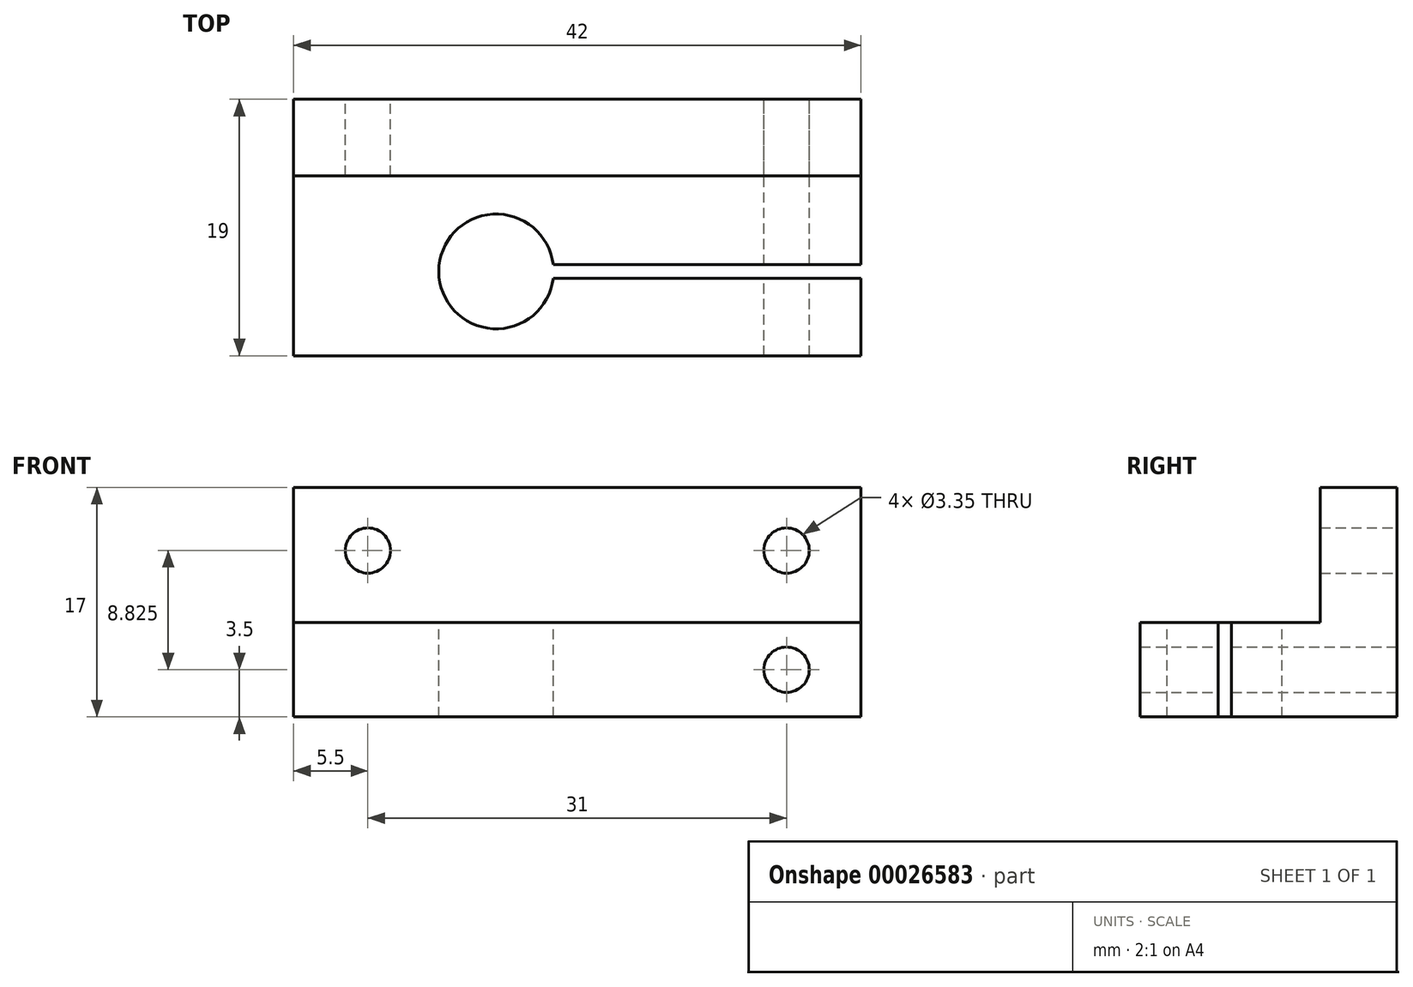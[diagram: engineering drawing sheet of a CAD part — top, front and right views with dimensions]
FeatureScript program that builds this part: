
annotation { "Feature Type Name" : "Feature", "Feature Type Description" : "" }
export const myFeature = defineFeature(function(context is Context, id is Id, definition is map)
    precondition{}
    {
        {
            var Q0;
            Q0=qCreatedBy(makeId("Top.planeOp"),FACE);
            var sketch = newSketch(context, id + "F0", { "sketchPlane" : qUnion([Q0])});
            skLineSegment(sketch, "E0.bottom", {"start": v(0, 0) * mm, "end": v(42, 0) * mm});
            skLineSegment(sketch, "E0.top", {"start": v(0, 19) * mm, "end": v(42, 19) * mm});
            skLineSegment(sketch, "E0.left", {"start": v(0, 0) * mm, "end": v(0, 19) * mm});
            skLineSegment(sketch, "E0.right", {"start": v(42, 0) * mm, "end": v(42, 19) * mm});
            skSolve(sketch);
        }
        {
            var Q0;
            Q0=qSketchRegion(id+"F0",true);
            extrude(context, id + "F1", {"entities" : qUnion([Q0]), "depth" : 7 * mm});
        }
        {
            var Q0;
            Q0=makeQuery(id+"F1.opExtrude","CAP_FACE",FACE,{"disambiguationData":[OSD([sQuery(id+"F0.wireOp",EDGE,"E0.bottom"),sQuery(id+"F0.wireOp",EDGE,"E0.top"),sQuery(id+"F0.wireOp",EDGE,"E0.left"),sQuery(id+"F0.wireOp",EDGE,"E0.right")])],"isStart":false});
            var sketch = newSketch(context, id + "F2", { "sketchPlane" : qUnion([Q0])});
            skCircle(sketch, "E1", {"center": v(15, 6.25) * mm, "radius": 4.25 * mm});
            skLineSegment(sketch, "E2", {"start": v(15, 6.25) * mm, "end": v(42, 6.25) * mm});
            skLineSegment(sketch, "E3", {"start": v(42, 6.25) * mm, "end": v(42, 5.75) * mm});
            skLineSegment(sketch, "E4", {"start": v(42, 5.75) * mm, "end": v(19.22, 5.75) * mm});
            skLineSegment(sketch, "E5", {"start": v(42, 6.25) * mm, "end": v(42, 6.75) * mm});
            skLineSegment(sketch, "E6", {"start": v(42, 6.75) * mm, "end": v(19.22, 6.75) * mm});
            skSolve(sketch);
        }
        {
            var Q0;
            Q0=makeQuery(id+"F1.opExtrude","SWEPT_FACE",FACE,{"disambiguationData":[OSD([sQuery(id+"F0.wireOp",EDGE,"E0.top")])]});
            var sketch = newSketch(context, id + "F3", { "sketchPlane" : qUnion([Q0])});
            skCircle(sketch, "E7", {"center": v(-36.5, 3.5) * mm, "radius": 1.68 * mm});
            skLineSegment(sketch, "E8", {"start": v(-36.5, 3.5) * mm, "end": v(-42, 3.5) * mm});
            skSolve(sketch);
        }
        {
            var Q0;
            Q0=qSketchRegion(id+"F3",true);
            extrude(context, id + "F4", {"entities" : qUnion([Q0]), "operationType" : NewBodyOperationType.REMOVE, "oppositeDirection" : true, "depth" : 25 * mm});
        }
        {
            var Q0;
            Q0=makeQuery(id+"F1.opExtrude","CAP_FACE",FACE,{"disambiguationData":[OSD([sQuery(id+"F0.wireOp",EDGE,"E0.bottom"),sQuery(id+"F0.wireOp",EDGE,"E0.top"),sQuery(id+"F0.wireOp",EDGE,"E0.left"),sQuery(id+"F0.wireOp",EDGE,"E0.right")])],"isStart":false});
            var sketch = newSketch(context, id + "F5", { "sketchPlane" : qUnion([Q0])});
            skLineSegment(sketch, "E9.bottom", {"start": v(0, 19) * mm, "end": v(42, 19) * mm});
            skLineSegment(sketch, "E9.top", {"start": v(0, 13.33) * mm, "end": v(42, 13.33) * mm});
            skLineSegment(sketch, "E9.left", {"start": v(0, 19) * mm, "end": v(0, 13.33) * mm});
            skLineSegment(sketch, "E9.right", {"start": v(42, 19) * mm, "end": v(42, 13.33) * mm});
            skSolve(sketch);
        }
        {
            var Q0;
            Q0=makeQuery(id+"F5.imprint","IMPRINT",FACE,{"disambiguationData":[TD([[makeQuery(id+"F5.imprint","IMPRINT",EDGE,{"derivedFrom":sQuery(id+"F5.wireOp",EDGE,"E9.bottom")}),-1.0]])]});
            extrude(context, id + "F6", {"entities" : qUnion([Q0]), "operationType" : NewBodyOperationType.ADD, "depth" : 10 * mm});
        }
        {
            var Q0;
            Q0=makeQuery(id+"F6.boolean.opBoolean","MERGE",FACE,{"derivedFrom":[makeQuery(id+"F1.opExtrude","SWEPT_FACE",FACE,{"disambiguationData":[OSD([sQuery(id+"F0.wireOp",EDGE,"E0.top")])]}),makeQuery(id+"F6.opExtrude","SWEPT_FACE",FACE,{"disambiguationData":[OSD([sQuery(id+"FFFDCbTcivKPk1C_1.wireOp",EDGE,"d29ae964-e38a-46b3-8ff4-cadffaec6662.bottom")])]})]});
            var sketch = newSketch(context, id + "F7", { "sketchPlane" : qUnion([Q0])});
            skPoint(sketch, "E10", {"position": v(-36.5, 3.5) * mm});
            skCircle(sketch, "E11", {"center": v(-36.5, 12.33) * mm, "radius": 1.68 * mm});
            skCircle(sketch, "E12", {"center": v(-5.5, 12.33) * mm, "radius": 1.68 * mm});
            skSolve(sketch);
        }
        {
            var Q0;
            Q0=qSketchRegion(id+"F7",true);
            extrude(context, id + "F8", {"entities" : qUnion([Q0]), "operationType" : NewBodyOperationType.REMOVE, "oppositeDirection" : true, "depth" : 25 * mm});
        }
        {
            var Q0;
            Q0=qSketchRegion(id+"F2",true);
            extrude(context, id + "F9", {"entities" : qUnion([Q0]), "operationType" : NewBodyOperationType.REMOVE, "oppositeDirection" : true, "depth" : 25 * mm});
        }
    });
